# Revit family: 50345_jumpuing_jet
name_source: partatom
category: Körper
revit_build: Autodesk Revit 2015 (Build: 20140606_1530(x64)
units: mm (PartAtom-declared; Revit-internal decimal feet)

## types (1)
- jumping Jet Rainbow Star / DMX/01
    Beschreibung = controllable Nozzles
    DMX connection = 1x
    Dimensions  LxWxH = 478x305x550 mm
    Hersteller = OASE GmbH Post Box 2069, 48469 Hörstel , Germany +49 5454 80-0
    Homepage = http://www.oase-livingwater.com
    Jet diameter = 12 mm
    Light type = LED RGB multiple spotlights
    Material = Plastic / stainless steel 1.4301 ( AISI 304 )
    Max. water depth = 300 mm
    Min. water depth = 200 mm
    Modell = jumping Jet Rainbow Star / DMX/01
    Name = jumping Jet Rainbow Star / DMX/01
    Pressure side connection = 1  inch
    Rated voltage, mechanical / illumination = 12 V/AC
    Vertical pivoting range = 45-90 °C
    Weight = 11 kg
    oder no. = 50345
    power consumption, mechanical / illumination = 33 W

## geometry (parser evidence)
native form markers: Blend x6
no freeform markers — native parametric forms only
